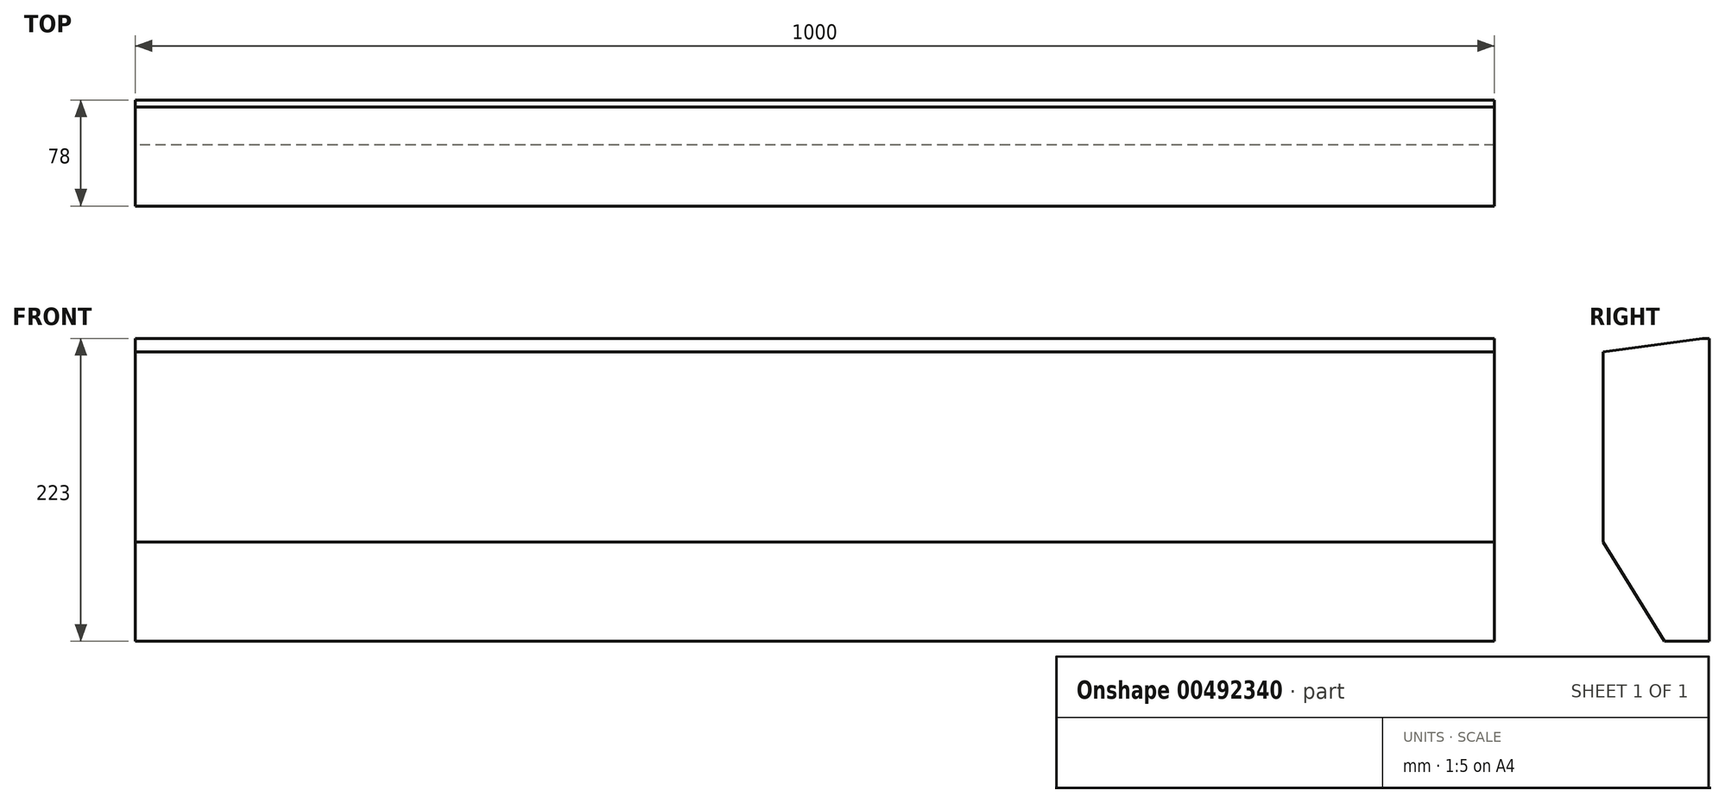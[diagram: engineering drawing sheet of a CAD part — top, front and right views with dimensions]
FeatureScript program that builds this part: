
annotation { "Feature Type Name" : "Feature", "Feature Type Description" : "" }
export const myFeature = defineFeature(function(context is Context, id is Id, definition is map)
    precondition{}
    {
        {
            var Q0;
            Q0=qCreatedBy(makeId("Right.planeOp"),FACE);
            var sketch = newSketch(context, id + "F0", { "sketchPlane" : qUnion([Q0])});
            skLineSegment(sketch, "E0.bottom", {"start": v(-41.7, 163.55) * mm, "end": v(36.3, 163.55) * mm});
            skLineSegment(sketch, "E0.top", {"start": v(-41.7, -59.45) * mm, "end": v(36.3, -59.45) * mm});
            skLineSegment(sketch, "E0.left", {"start": v(-41.7, 163.55) * mm, "end": v(-41.7, -59.45) * mm});
            skLineSegment(sketch, "E0.right", {"start": v(36.3, 163.55) * mm, "end": v(36.3, -59.45) * mm});
            skSolve(sketch);
        }
        {
            var Q0;
            Q0=makeQuery(id+"F0.imprint","IMPRINT",FACE,{"disambiguationData":[TD([[makeQuery(id+"F0.imprint","IMPRINT",EDGE,{"derivedFrom":sQuery(id+"F0.wireOp",EDGE,"E0.bottom")}),-1.0]])]});
            extrude(context, id + "F1", {"entities" : qUnion([Q0]), "depth" : 1000 * mm});
        }
        {
            var Q0;
            Q0=makeQuery(id+"F1.opExtrude","SWEPT_EDGE",EDGE,{"disambiguationData":[OSD([sQuery(id+"F0.wireOp",EDGE,"E0.bottom"),sQuery(id+"F0.wireOp",EDGE,"E0.left")])]});
            chamfer(context, id + "F2", {"entities" : qUnion([Q0]), "chamferType" : ChamferType.TWO_OFFSETS, "width1" : 10 * mm, "oppositeDirection" : false, "width2" : 73 * mm, "tangentPropagation" : true});
        }
        {
            var Q0;
            Q0=makeQuery(id+"F1.opExtrude","SWEPT_EDGE",EDGE,{"disambiguationData":[OSD([sQuery(id+"F0.wireOp",EDGE,"E0.top"),sQuery(id+"F0.wireOp",EDGE,"E0.left")])]});
            chamfer(context, id + "F3", {"entities" : qUnion([Q0]), "chamferType" : ChamferType.TWO_OFFSETS, "width1" : 45 * mm, "oppositeDirection" : false, "width2" : 73 * mm, "tangentPropagation" : true});
        }
    });
